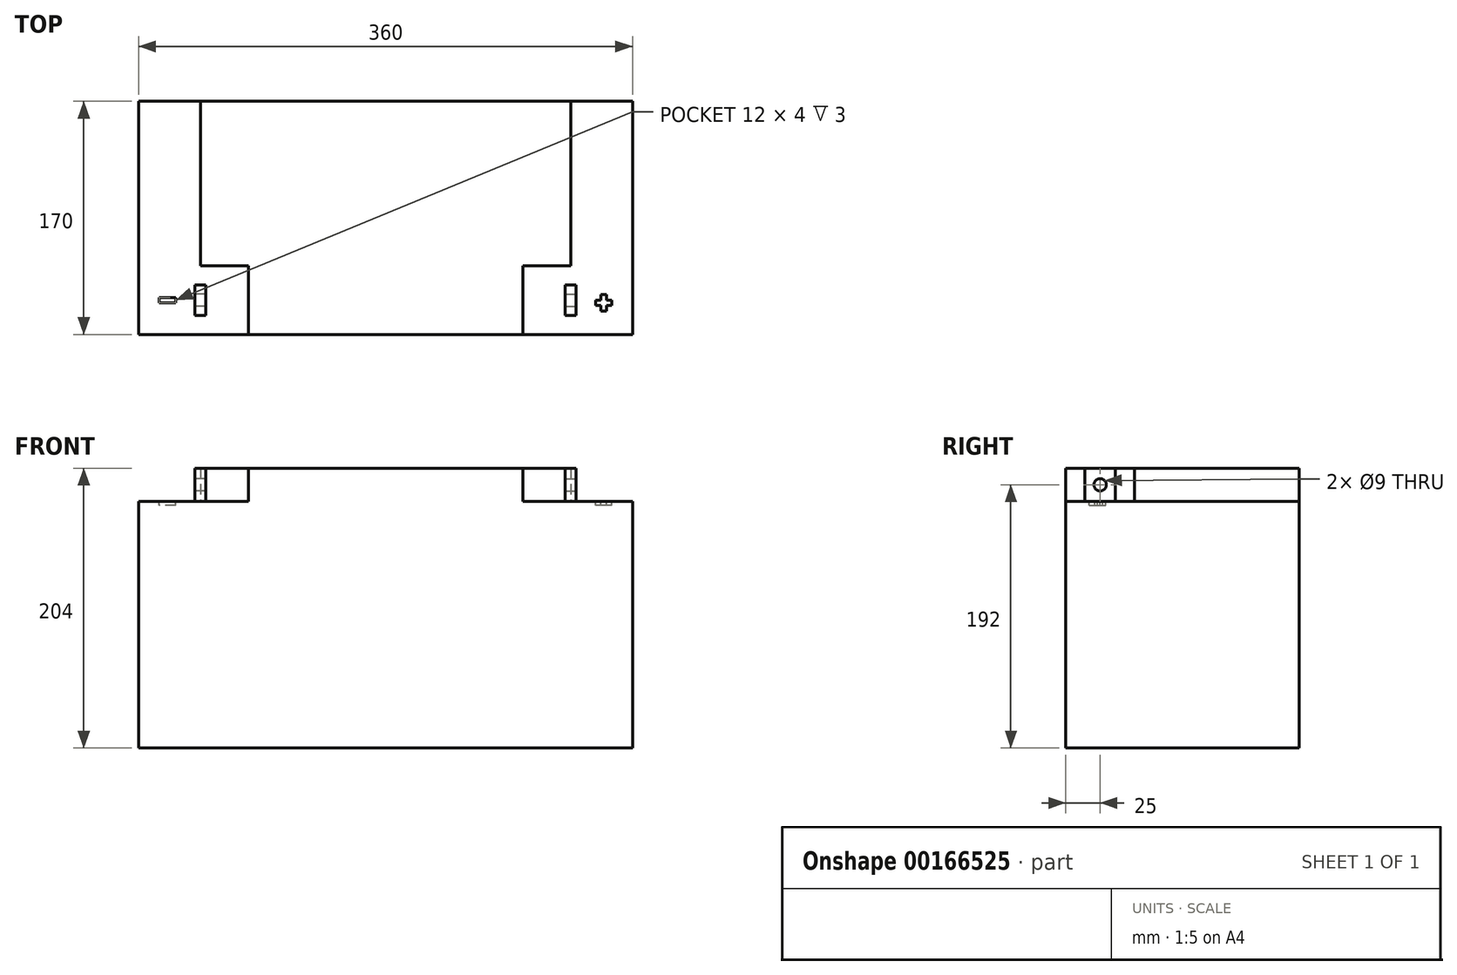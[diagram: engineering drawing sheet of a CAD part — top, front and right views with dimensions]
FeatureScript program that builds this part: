
annotation { "Feature Type Name" : "Feature", "Feature Type Description" : "" }
export const myFeature = defineFeature(function(context is Context, id is Id, definition is map)
    precondition{}
    {
        {
            var Q0;
            Q0=qCreatedBy(makeId("Top.planeOp"),FACE);
            var sketch = newSketch(context, id + "F0", { "sketchPlane" : qUnion([Q0])});
            skLineSegment(sketch, "E0.bottom", {"start": v(180, -85) * mm, "end": v(-180, -85) * mm});
            skLineSegment(sketch, "E0.top", {"start": v(180, 85) * mm, "end": v(-180, 85) * mm});
            skLineSegment(sketch, "E0.left", {"start": v(180, -85) * mm, "end": v(180, 85) * mm});
            skLineSegment(sketch, "E0.right", {"start": v(-180, -85) * mm, "end": v(-180, 85) * mm});
            skPoint(sketch, "E0.middle", {"position": v(0, 0) * mm});
            skSolve(sketch);
        }
        {
            var Q0;
            Q0=makeQuery(id+"F0.imprint","IMPRINT",FACE,{"disambiguationData":[TD([[makeQuery(id+"F0.imprint","IMPRINT",EDGE,{"derivedFrom":sQuery(id+"F0.wireOp",EDGE,"E0.bottom")}),-1.0]])]});
            extrude(context, id + "F1", {"entities" : qUnion([Q0]), "depth" : 180 * mm});
        }
        {
            var Q0;
            Q0=makeQuery(id+"F1.opExtrude","CAP_FACE",FACE,{"disambiguationData":[OSD([sQuery(id+"F0.wireOp",EDGE,"E0.bottom"),sQuery(id+"F0.wireOp",EDGE,"E0.top"),sQuery(id+"F0.wireOp",EDGE,"E0.left"),sQuery(id+"F0.wireOp",EDGE,"E0.right")])],"isStart":false});
            var sketch = newSketch(context, id + "F2", { "sketchPlane" : qUnion([Q0])});
            skLineSegment(sketch, "E1", {"start": v(0, 85) * mm, "end": v(0, -85) * mm, "construction": true});
            skLineSegment(sketch, "E2", {"start": v(0, -85) * mm, "end": v(-100, -85) * mm});
            skLineSegment(sketch, "E3", {"start": v(-100, -85) * mm, "end": v(-100, -35) * mm});
            skLineSegment(sketch, "E4", {"start": v(-100, -35) * mm, "end": v(-135, -35) * mm});
            skLineSegment(sketch, "E5", {"start": v(-135, -35) * mm, "end": v(-135, 85) * mm});
            skLineSegment(sketch, "E6", {"start": v(-135, 85) * mm, "end": v(0, 85) * mm});
            skLineSegment(sketch, "E7", {"start": v(-180, -60) * mm, "end": v(-135, -60) * mm, "construction": true});
            skLineSegment(sketch, "E8", {"start": v(-135, -60) * mm, "end": v(-135, -85) * mm, "construction": true});
            skLineSegment(sketch, "E9.bottom", {"start": v(-131, -71) * mm, "end": v(-139, -71) * mm});
            skLineSegment(sketch, "E9.top", {"start": v(-131, -49) * mm, "end": v(-139, -49) * mm});
            skLineSegment(sketch, "E9.left", {"start": v(-131, -71) * mm, "end": v(-131, -49) * mm});
            skLineSegment(sketch, "E9.right", {"start": v(-139, -71) * mm, "end": v(-139, -49) * mm});
            skPoint(sketch, "E9.middle", {"position": v(-135, -60) * mm});
            skLineSegment(sketch, "E10.MirrorCS", {"start": v(135, 85) * mm, "end": v(0, 85) * mm});
            skLineSegment(sketch, "E11.MirrorCS", {"start": v(135, -35) * mm, "end": v(135, 85) * mm});
            skLineSegment(sketch, "E12.MirrorCS", {"start": v(0, -85) * mm, "end": v(100, -85) * mm});
            skLineSegment(sketch, "E13.MirrorCS", {"start": v(100, -85) * mm, "end": v(100, -35) * mm});
            skLineSegment(sketch, "E14.MirrorCS", {"start": v(100, -35) * mm, "end": v(135, -35) * mm});
            skLineSegment(sketch, "E15.MirrorCS", {"start": v(131, -71) * mm, "end": v(131, -49) * mm});
            skLineSegment(sketch, "E16.MirrorCS", {"start": v(131, -71) * mm, "end": v(139, -71) * mm});
            skLineSegment(sketch, "E17.MirrorCS", {"start": v(131, -49) * mm, "end": v(139, -49) * mm});
            skLineSegment(sketch, "E18.MirrorCS", {"start": v(139, -71) * mm, "end": v(139, -49) * mm});
            skSolve(sketch);
        }
        {
            var Q0;
            Q0=makeQuery(id+"F2.imprint","IMPRINT",FACE,{"disambiguationData":[TD([[makeQuery(id+"F2.imprint","IMPRINT",EDGE,{"derivedFrom":sQuery(id+"F2.wireOp",EDGE,"E2")}),-1.0]])]});
            var Q1;
            Q1=makeQuery(id+"F2.imprint","IMPRINT",FACE,{"disambiguationData":[TD([[makeQuery(id+"F2.imprint","IMPRINT",EDGE,{"derivedFrom":sQuery(id+"F2.wireOp",EDGE,"E9.bottom")}),-1.0]])]});
            var Q2;
            Q2=makeQuery(id+"F2.imprint","IMPRINT",FACE,{"disambiguationData":[TD([[makeQuery(id+"F2.imprint","IMPRINT",EDGE,{"derivedFrom":sQuery(id+"F2.wireOp",EDGE,"E15.MirrorCS")}),-1.0]])]});
            extrude(context, id + "F3", {"entities" : qUnion([Q0, Q1, Q2]), "operationType" : NewBodyOperationType.ADD, "depth" : 24 * mm});
        }
        {
            var Q0;
            Q0=makeQuery(id+"F3.opExtrude","SWEPT_FACE",FACE,{"disambiguationData":[OSD([sQuery(id+"F2.wireOp",EDGE,"E9.right")])]});
            var sketch = newSketch(context, id + "F4", { "sketchPlane" : qUnion([Q0])});
            skLineSegment(sketch, "E19", {"start": v(49, 204) * mm, "end": v(71, 180) * mm, "construction": true});
            skLineSegment(sketch, "E20", {"start": v(71, 204) * mm, "end": v(49, 180) * mm, "construction": true});
            skCircle(sketch, "E21", {"center": v(60, 192) * mm, "radius": 4.5 * mm});
            skSolve(sketch);
        }
        {
            var Q0;
            Q0=makeQuery(id+"F4.imprint","IMPRINT",FACE,{"disambiguationData":[TD([[makeQuery(id+"F4.imprint","IMPRINT",EDGE,{"derivedFrom":sQuery(id+"F4.wireOp",EDGE,"E21")}),1.0]])]});
            extrude(context, id + "F5", {"entities" : qUnion([Q0]), "operationType" : NewBodyOperationType.REMOVE, "oppositeDirection" : true, "depth" : 25 * mm});
        }
        {
            var Q0;
            Q0=makeQuery(id+"F3.opExtrude","SWEPT_FACE",FACE,{"disambiguationData":[OSD([sQuery(id+"F2.wireOp",EDGE,"E18.MirrorCS")])]});
            var sketch = newSketch(context, id + "F6", { "sketchPlane" : qUnion([Q0])});
            skLineSegment(sketch, "E22", {"start": v(-49, 204) * mm, "end": v(-71, 180) * mm, "construction": true});
            skLineSegment(sketch, "E23", {"start": v(-71, 204) * mm, "end": v(-49, 180) * mm, "construction": true});
            skCircle(sketch, "E24", {"center": v(-60, 192) * mm, "radius": 4.5 * mm});
            skSolve(sketch);
        }
        {
            var Q0;
            Q0=makeQuery(id+"F6.imprint","IMPRINT",FACE,{"disambiguationData":[TD([[makeQuery(id+"F6.imprint","IMPRINT",EDGE,{"derivedFrom":sQuery(id+"F6.wireOp",EDGE,"E24")}),1.0]])]});
            extrude(context, id + "F7", {"entities" : qUnion([Q0]), "operationType" : NewBodyOperationType.REMOVE, "oppositeDirection" : true, "depth" : 25 * mm});
        }
        {
            var Q0;
            {var subQ0=sQuery(id+"F0.wireOp",EDGE,"E0.bottom");var subQ1=sQuery(id+"F0.wireOp",EDGE,"E0.top");var subQ2=sQuery(id+"F0.wireOp",EDGE,"E0.right");Q0=makeQuery(id+"F3.boolean.opBoolean","SPLIT",FACE,{"disambiguationData":[TD([makeQuery(id+"F1.opExtrude","SWEPT_FACE",FACE,{"disambiguationData":[OSD([subQ2])]})])],"derivedFrom":makeQuery(id+"F1.opExtrude","CAP_FACE",FACE,{"disambiguationData":[OSD([subQ0,subQ1,sQuery(id+"F0.wireOp",EDGE,"E0.left"),subQ2])],"isStart":false})});}
            var sketch = newSketch(context, id + "F8", { "sketchPlane" : qUnion([Q0])});
            skLineSegment(sketch, "E25", {"start": v(-139, -60) * mm, "end": v(-159, -60) * mm, "construction": true});
            skLineSegment(sketch, "E26.bottom", {"start": v(-153, -62) * mm, "end": v(-165, -62) * mm});
            skLineSegment(sketch, "E26.top", {"start": v(-153, -58) * mm, "end": v(-165, -58) * mm});
            skLineSegment(sketch, "E26.left", {"start": v(-153, -62) * mm, "end": v(-153, -58) * mm});
            skLineSegment(sketch, "E26.right", {"start": v(-165, -62) * mm, "end": v(-165, -58) * mm});
            skPoint(sketch, "E26.middle", {"position": v(-159, -60) * mm});
            skSolve(sketch);
        }
        {
            var Q0;
            {var subQ0=sQuery(id+"F0.wireOp",EDGE,"E0.bottom");var subQ1=sQuery(id+"F0.wireOp",EDGE,"E0.top");var subQ2=sQuery(id+"F0.wireOp",EDGE,"E0.left");Q0=makeQuery(id+"F3.boolean.opBoolean","SPLIT",FACE,{"disambiguationData":[TD([makeQuery(id+"F1.opExtrude","SWEPT_FACE",FACE,{"disambiguationData":[OSD([subQ2])]})])],"derivedFrom":makeQuery(id+"F1.opExtrude","CAP_FACE",FACE,{"disambiguationData":[OSD([subQ0,subQ1,subQ2,sQuery(id+"F0.wireOp",EDGE,"E0.right")])],"isStart":false})});}
            var sketch = newSketch(context, id + "F9", { "sketchPlane" : qUnion([Q0])});
            skLineSegment(sketch, "E27", {"start": v(139, -61.88) * mm, "end": v(159, -61.88) * mm, "construction": true});
            skLineSegment(sketch, "E28.bottom", {"start": v(165, -63.88) * mm, "end": v(153, -63.88) * mm});
            skLineSegment(sketch, "E28.top", {"start": v(165, -59.88) * mm, "end": v(153, -59.88) * mm});
            skLineSegment(sketch, "E28.left", {"start": v(165, -63.88) * mm, "end": v(165, -59.88) * mm});
            skLineSegment(sketch, "E28.right", {"start": v(153, -63.88) * mm, "end": v(153, -59.88) * mm});
            skPoint(sketch, "E28.middle", {"position": v(159, -61.88) * mm});
            skLineSegment(sketch, "E29.bottom", {"start": v(161, -67.88) * mm, "end": v(157, -67.88) * mm});
            skLineSegment(sketch, "E29.top", {"start": v(161, -55.88) * mm, "end": v(157, -55.88) * mm});
            skLineSegment(sketch, "E29.left", {"start": v(161, -67.88) * mm, "end": v(161, -55.88) * mm});
            skLineSegment(sketch, "E29.right", {"start": v(157, -67.88) * mm, "end": v(157, -55.88) * mm});
            skSolve(sketch);
        }
        {
            var Q0;
            Q0=makeQuery(id+"F8.imprint","IMPRINT",FACE,{"disambiguationData":[TD([[makeQuery(id+"F8.imprint","IMPRINT",EDGE,{"derivedFrom":sQuery(id+"F8.wireOp",EDGE,"E26.bottom")}),-1.0]])]});
            var Q1;
            {var subQ0=sQuery(id+"F9.wireOp",EDGE,"E28.right");Q1=makeQuery(id+"F9.imprint","IMPRINT",FACE,{"disambiguationData":[TD([[makeQuery(id+"F9.imprint","IMPRINT",EDGE,{"derivedFrom":subQ0}),-1.0]])]});}
            var Q2;
            {var subQ0=sQuery(id+"F9.wireOp",EDGE,"E29.left");var subQ1=sQuery(id+"F9.wireOp",EDGE,"E28.bottom");var subQ2=makeQuery(id+"F9.imprint","INTERSECT",VERTEX,{"derivedFrom":[subQ1,subQ0]});Q2=makeQuery(id+"F9.imprint","IMPRINT",FACE,{"disambiguationData":[TD([[makeQuery(id+"F9.imprint","IMPRINT",EDGE,{"disambiguationData":[TD([[subQ2,-1.0]])],"derivedFrom":subQ1}),-1.0]])]});}
            var Q3;
            {var subQ0=sQuery(id+"F9.wireOp",EDGE,"E28.left");Q3=makeQuery(id+"F9.imprint","IMPRINT",FACE,{"disambiguationData":[TD([[makeQuery(id+"F9.imprint","IMPRINT",EDGE,{"derivedFrom":subQ0}),1.0]])]});}
            var Q4;
            {var subQ5=sQuery(id+"F9.wireOp",EDGE,"E29.top");Q4=makeQuery(id+"F9.imprint","IMPRINT",FACE,{"disambiguationData":[TD([[makeQuery(id+"F9.imprint","IMPRINT",EDGE,{"derivedFrom":subQ5}),1.0]])]});}
            var Q5;
            {var subQ5=sQuery(id+"F9.wireOp",EDGE,"E29.bottom");Q5=makeQuery(id+"F9.imprint","IMPRINT",FACE,{"disambiguationData":[TD([[makeQuery(id+"F9.imprint","IMPRINT",EDGE,{"derivedFrom":subQ5}),-1.0]])]});}
            extrude(context, id + "F10", {"entities" : qUnion([Q0, Q1, Q2, Q3, Q4, Q5]), "operationType" : NewBodyOperationType.REMOVE, "oppositeDirection" : true, "depth" : 3 * mm});
        }
    });
